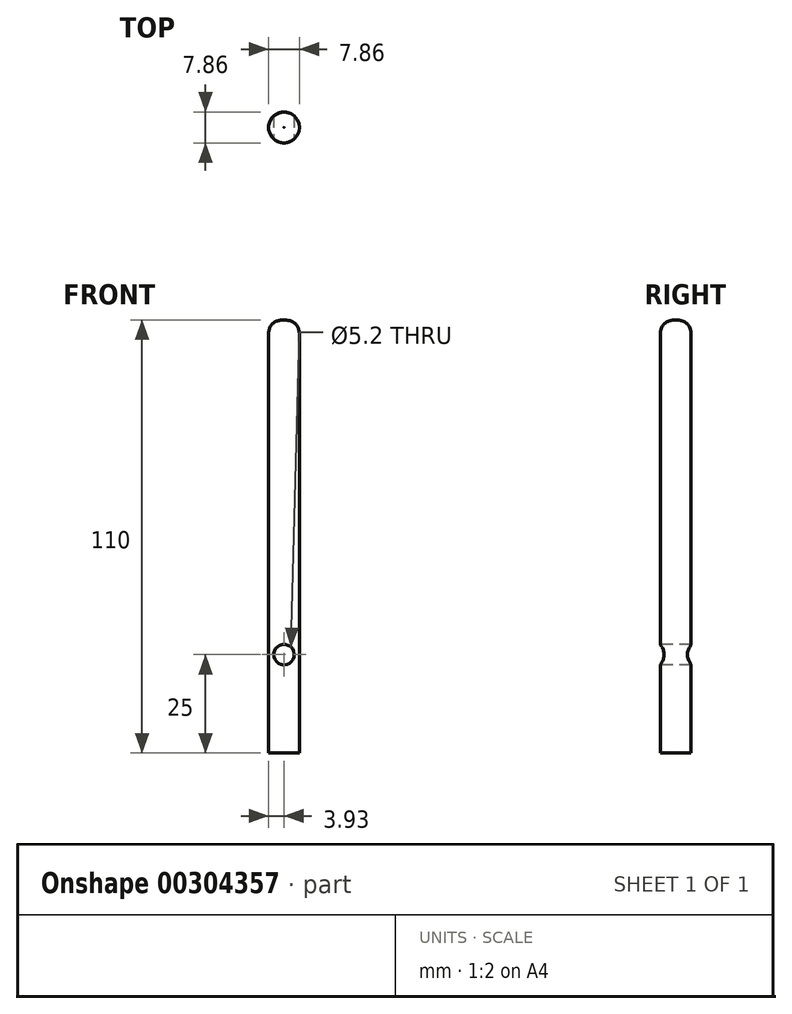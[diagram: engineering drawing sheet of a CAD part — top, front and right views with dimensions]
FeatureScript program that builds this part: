
annotation { "Feature Type Name" : "Feature", "Feature Type Description" : "" }
export const myFeature = defineFeature(function(context is Context, id is Id, definition is map)
    precondition{}
    {
        {
            var Q0;
            Q0=qCreatedBy(makeId("Top.planeOp"),FACE);
            var sketch = newSketch(context, id + "F0", { "sketchPlane" : qUnion([Q0])});
            skCircle(sketch, "E0", {"center": v(0, 0) * mm, "radius": 3.93 * mm});
            skSolve(sketch);
        }
        {
            var Q0;
            Q0=makeQuery(id+"F0.imprint","IMPRINT",FACE,{"disambiguationData":[TD([[makeQuery(id+"F0.imprint","IMPRINT",EDGE,{"derivedFrom":sQuery(id+"F0.wireOp",EDGE,"E0")}),1.0]])]});
            extrude(context, id + "F1", {"entities" : qUnion([Q0]), "depth" : 110 * mm});
        }
        {
            var Q0;
            Q0=makeQuery(id+"F1.opExtrude","CAP_EDGE",EDGE,{"disambiguationData":[OSD([sQuery(id+"F0.wireOp",EDGE,"E0")])],"isStart":false});
            fillet(context, id + "F2", {"entities" : qUnion([Q0]), "radius" : 3.9 * mm, "tangentPropagation" : true, "rho" : 0.5, "crossSection" : FilletCrossSection.CONIC, "allowEdgeOverflow" : false});
        }
        {
            var Q0;
            Q0=qCreatedBy(makeId("Front.planeOp"),FACE);
            var sketch = newSketch(context, id + "F3", { "sketchPlane" : qUnion([Q0])});
            skPoint(sketch, "E1", {"position": v(0, 25) * mm});
            skCircle(sketch, "E2", {"center": v(0, 25) * mm, "radius": 2.6 * mm});
            skSolve(sketch);
        }
        {
            var Q0;
            Q0=makeQuery(id+"F3.imprint","IMPRINT",FACE,{"disambiguationData":[TD([[makeQuery(id+"F3.imprint","IMPRINT",EDGE,{"derivedFrom":sQuery(id+"F3.wireOp",EDGE,"E2")}),1.0]])]});
            extrude(context, id + "F4", {"entities" : qUnion([Q0]), "operationType" : NewBodyOperationType.REMOVE, "endBound" : BoundingType.THROUGH_ALL, "oppositeDirection" : true, "depth" : 25 * mm, "hasSecondDirection" : true, "secondDirectionBound" : SecondDirectionBoundingType.THROUGH_ALL, "secondDirectionOppositeDirection" : false, "secondDirectionDepth" : 25 * mm});
        }
    });
